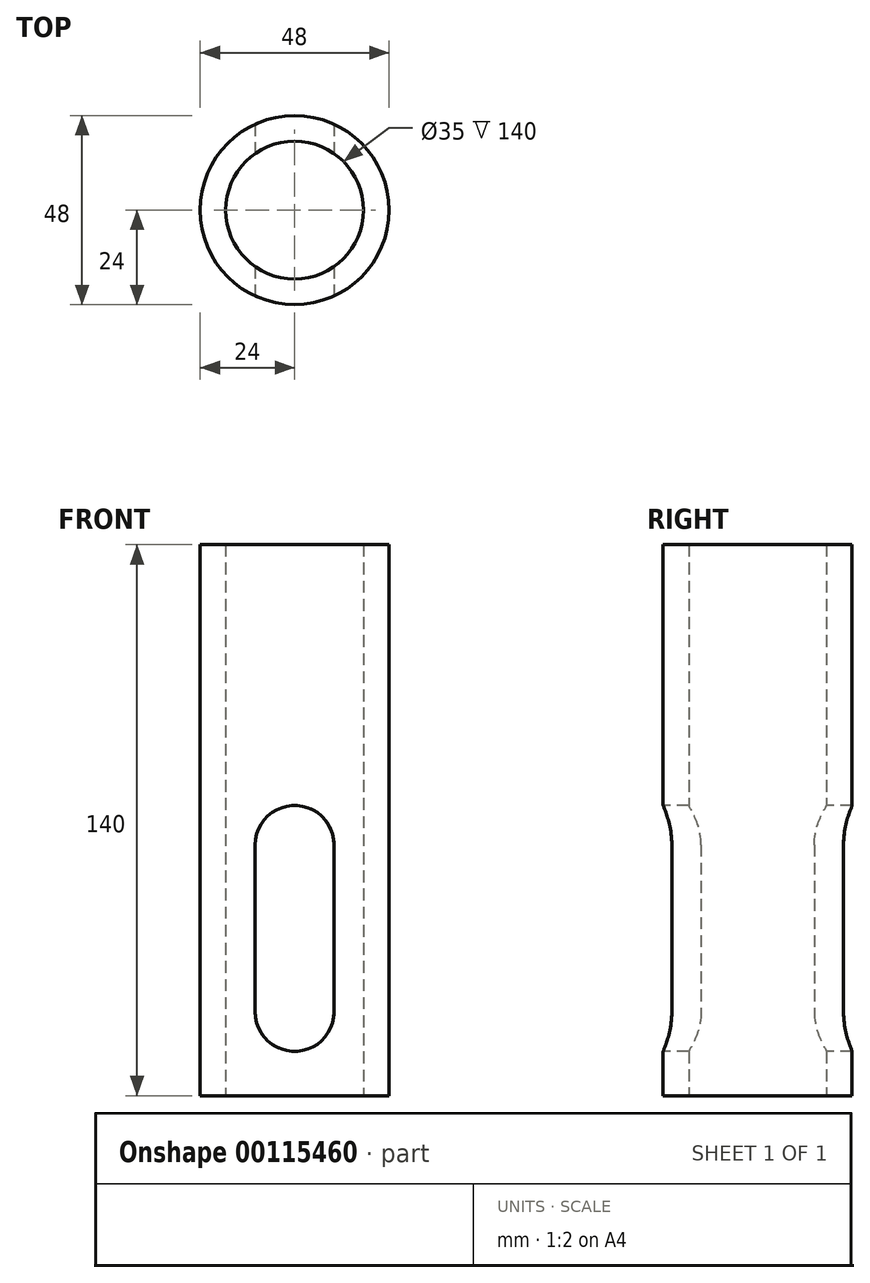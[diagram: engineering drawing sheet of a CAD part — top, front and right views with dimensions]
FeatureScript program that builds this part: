
annotation { "Feature Type Name" : "Feature", "Feature Type Description" : "" }
export const myFeature = defineFeature(function(context is Context, id is Id, definition is map)
    precondition{}
    {
        {
            var Q0;
            Q0=qCreatedBy(makeId("Top.planeOp"),FACE);
            var sketch = newSketch(context, id + "F0", { "sketchPlane" : qUnion([Q0])});
            skCircle(sketch, "E0", {"center": v(0, 0) * mm, "radius": 24 * mm});
            skCircle(sketch, "E1", {"center": v(0, 0) * mm, "radius": 17.5 * mm});
            skSolve(sketch);
        }
        {
            var Q0;
            Q0=makeQuery(id+"F0.imprint","IMPRINT",FACE,{"disambiguationData":[TD([[makeQuery(id+"F0.imprint","IMPRINT",EDGE,{"derivedFrom":sQuery(id+"F0.wireOp",EDGE,"E0")}),1.0]])]});
            extrude(context, id + "F1", {"entities" : qUnion([Q0]), "depth" : 140 * mm});
        }
        {
            var Q0;
            Q0=qCreatedBy(makeId("Front.planeOp"),FACE);
            var sketch = newSketch(context, id + "F2", { "sketchPlane" : qUnion([Q0])});
            skLineSegment(sketch, "E2", {"start": v(0, 0) * mm, "end": v(0, 42.5) * mm, "construction": true});
            skLineSegment(sketch, "E3.bottom", {"start": v(10, 21.25) * mm, "end": v(-10, 21.25) * mm, "construction": true});
            skLineSegment(sketch, "E3.top", {"start": v(10, 63.75) * mm, "end": v(-10, 63.75) * mm, "construction": true});
            skLineSegment(sketch, "E3.left", {"start": v(10, 21.25) * mm, "end": v(10, 63.75) * mm});
            skLineSegment(sketch, "E3.right", {"start": v(-10, 21.25) * mm, "end": v(-10, 63.75) * mm});
            skPoint(sketch, "E3.middle", {"position": v(0, 42.5) * mm});
            skArc(sketch, "E4", {"start": v(10, 63.75) * mm, "mid": v(0, 73.75) * mm, "end": v(-10, 63.75) * mm});
            skArc(sketch, "E5", {"start": v(-10, 21.25) * mm, "mid": v(0, 11.25) * mm, "end": v(10, 21.25) * mm});
            skSolve(sketch);
        }
        {
            var Q0;
            Q0 = qSketchRegion(id + "F2", true);
            extrude(context, id + "F3", {"entities" : qUnion([Q0]), "operationType" : NewBodyOperationType.REMOVE, "endBound" : BoundingType.THROUGH_ALL, "oppositeDirection" : true, "depth" : 25.4 * mm, "hasSecondDirection" : true, "secondDirectionBound" : SecondDirectionBoundingType.THROUGH_ALL, "secondDirectionOppositeDirection" : false, "secondDirectionDepth" : 25.4 * mm});
        }
    });
